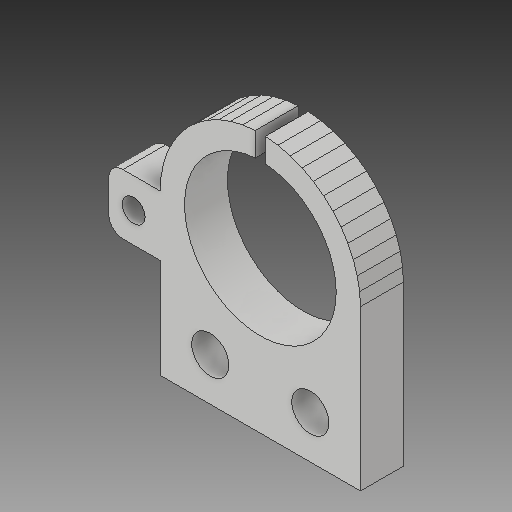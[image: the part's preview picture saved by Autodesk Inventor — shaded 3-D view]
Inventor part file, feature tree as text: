
AUTODESK INVENTOR PART (.ipt)
format: ipt  version: 2018 (Build 220112000, 112)  size: 182,784 bytes
history: native  units: mm
features: other x3, sketch x2
ambient origin geometry x8: Origin, YZ Plane, XZ Plane, XY Plane, X Axis, Y Axis, Z Axis, Center Point
bodies: Solid1 (feature_tree)
feature tree (5):
  other  "Left Bed Holder Upper.ipt"
  other  "Solid1::Left Bed Holder Upper.ipt"
  other  "TaggingFeature1"
  sketch  "Sketch1"  dims[d0=10.0mm]
  sketch  "Sketch3"
